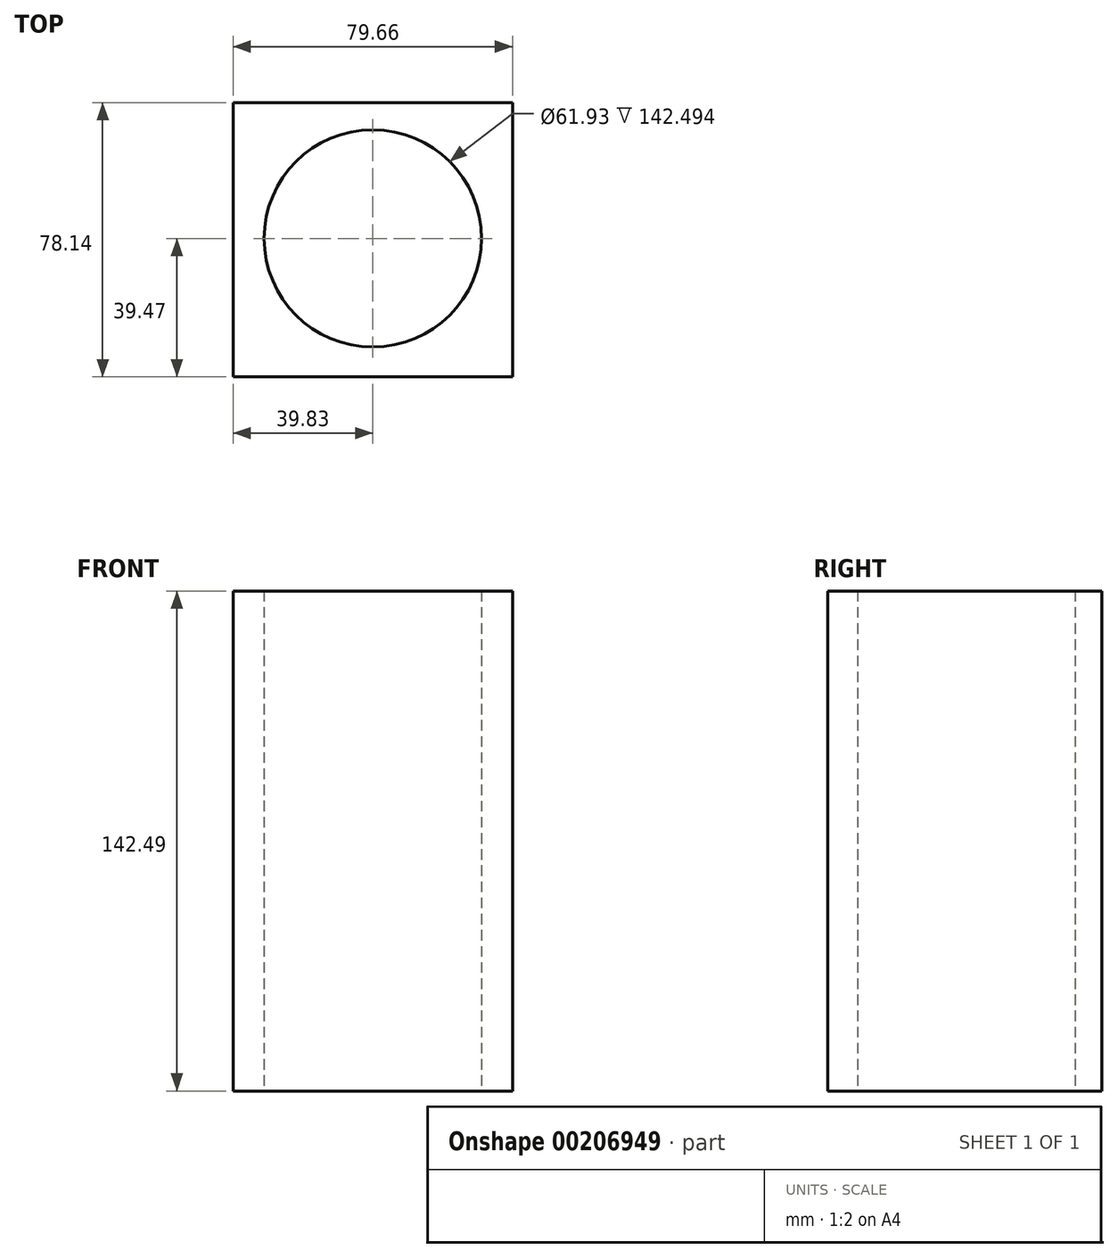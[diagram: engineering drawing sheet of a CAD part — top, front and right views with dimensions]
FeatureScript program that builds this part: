
annotation { "Feature Type Name" : "Feature", "Feature Type Description" : "" }
export const myFeature = defineFeature(function(context is Context, id is Id, definition is map)
    precondition{}
    {
        {
            var Q0;
            Q0=qCreatedBy(makeId("Top.planeOp"),FACE);
            var sketch = newSketch(context, id + "F0", { "sketchPlane" : qUnion([Q0])});
            skLineSegment(sketch, "E0.bottom", {"start": v(-54.45, -39.47) * mm, "end": v(25.2, -39.47) * mm});
            skLineSegment(sketch, "E0.top", {"start": v(-54.45, 38.67) * mm, "end": v(25.2, 38.67) * mm});
            skLineSegment(sketch, "E0.left", {"start": v(-54.45, -39.47) * mm, "end": v(-54.45, 38.67) * mm});
            skLineSegment(sketch, "E0.right", {"start": v(25.2, -39.47) * mm, "end": v(25.2, 38.67) * mm});
            skCircle(sketch, "E1", {"center": v(-14.62, 0) * mm, "radius": 30.96 * mm});
            skSolve(sketch);
        }
        {
            var Q0;
            Q0=makeQuery(id+"F0.imprint","IMPRINT",FACE,{"disambiguationData":[TD([[makeQuery(id+"F0.imprint","IMPRINT",EDGE,{"derivedFrom":sQuery(id+"F0.wireOp",EDGE,"E0.bottom")}),1.0]])]});
            extrude(context, id + "F1", {"entities" : qUnion([Q0]), "depth" : 142.5 * mm});
        }
    });
